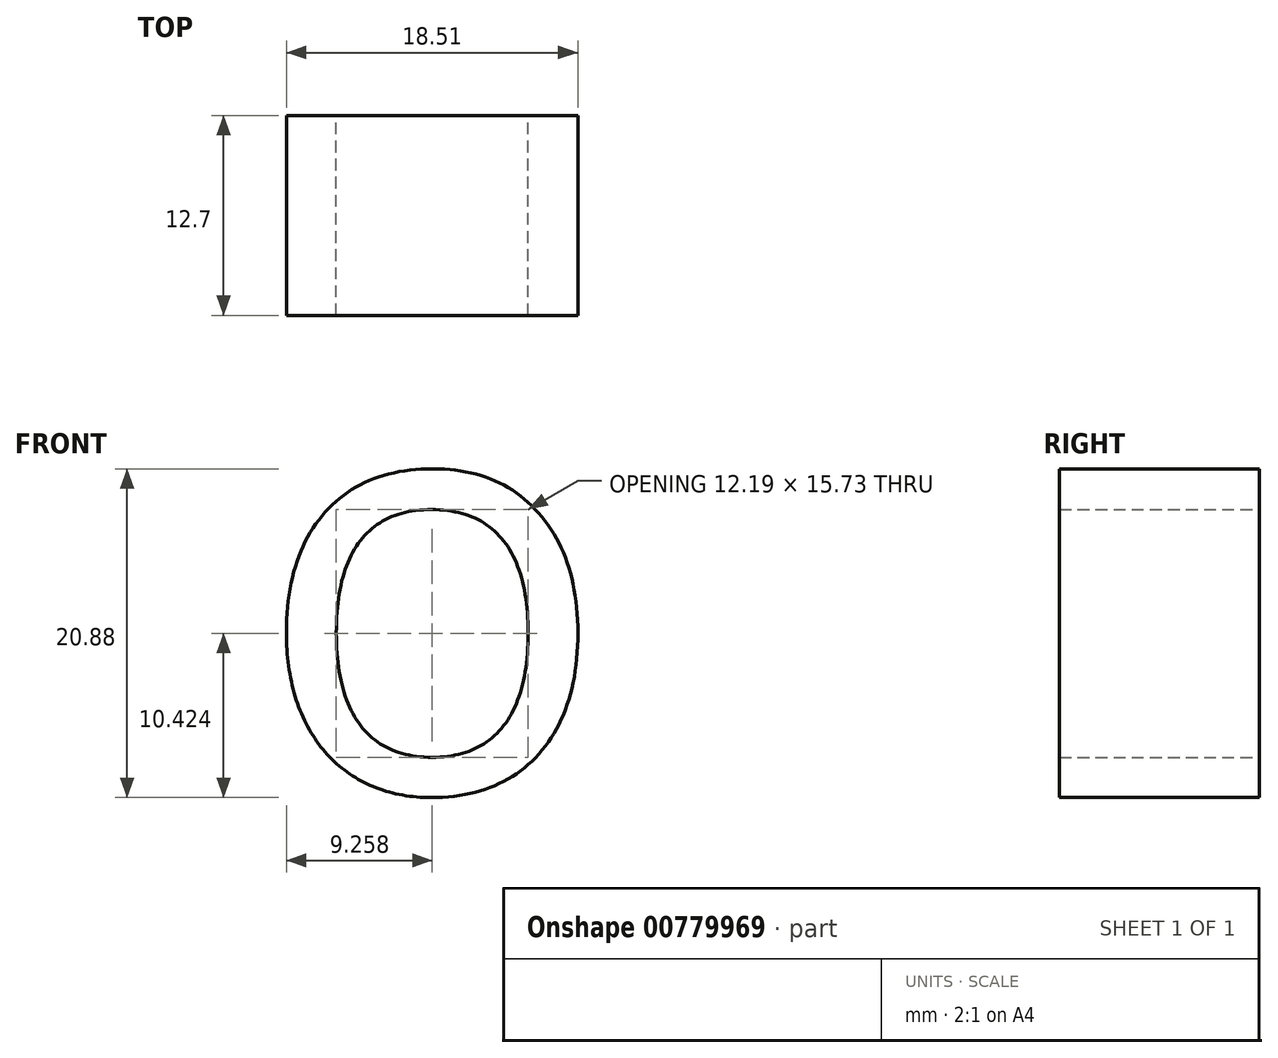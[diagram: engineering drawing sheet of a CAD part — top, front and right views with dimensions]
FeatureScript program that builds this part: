
annotation { "Feature Type Name" : "Feature", "Feature Type Description" : "" }
export const myFeature = defineFeature(function(context is Context, id is Id, definition is map)
    precondition{}
    {
        {
            var Q0;
            Q0=qCreatedBy(makeId("Front.planeOp"),FACE);
            var sketch = newSketch(context, id + "F0", { "sketchPlane" : qUnion([Q0])});
            skText(sketch, "E0", { "text": "o", "fontName": "OpenSans-Regular.ttf"});
            const initialGuessF0  = {"E0": [-0.05467, 0, 1, 0, 0.0271]};
            skSetInitialGuess(sketch, initialGuessF0);
            skSolve(sketch);
        }
        {
            var Q0;
            Q0 = qSketchRegion(id + "F0", true);
            extrude(context, id + "F1", {"entities" : qUnion([Q0]), "depth" : 12.7 * mm, "offsetDistance" : 25.4 * mm});
        }
    });
